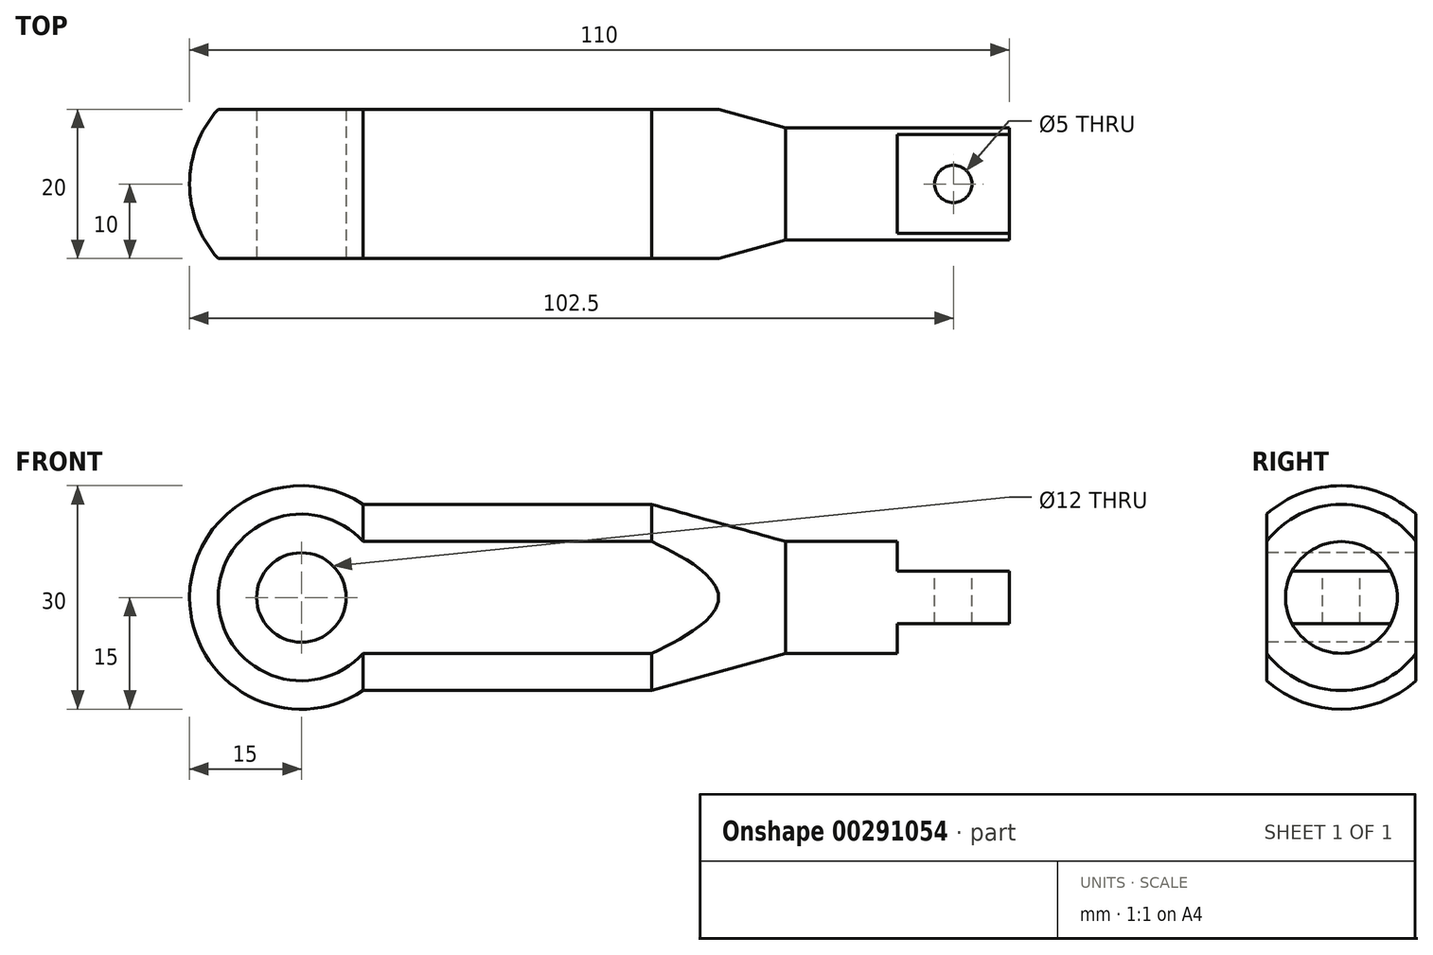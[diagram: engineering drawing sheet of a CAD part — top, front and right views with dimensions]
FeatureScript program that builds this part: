
annotation { "Feature Type Name" : "Feature", "Feature Type Description" : "" }
export const myFeature = defineFeature(function(context is Context, id is Id, definition is map)
    precondition{}
    {
        {
            var Q0;
            Q0=qCreatedBy(makeId("Front.planeOp"),FACE);
            var sketch = newSketch(context, id + "F0", { "sketchPlane" : qUnion([Q0])});
            skLineSegment(sketch, "E0", {"start": v(0, 0) * mm, "end": v(148.34, 0) * mm, "construction": true});
            skArc(sketch, "E1", {"start": v(-15, 0) * mm, "mid": v(-7.1, 13.22) * mm, "end": v(8.3, 12.5) * mm});
            skLineSegment(sketch, "E2", {"start": v(8.3, 12.5) * mm, "end": v(47, 12.5) * mm});
            skLineSegment(sketch, "E3", {"start": v(47, 12.5) * mm, "end": v(65, 7.5) * mm});
            skLineSegment(sketch, "E4", {"start": v(65, 7.5) * mm, "end": v(95, 7.5) * mm});
            skLineSegment(sketch, "E5", {"start": v(95, 7.5) * mm, "end": v(95, 0) * mm});
            skLineSegment(sketch, "E6", {"start": v(95, 0) * mm, "end": v(-15, 0) * mm});
            skSolve(sketch);
        }
        {
            var Q0;
            Q0 = qSketchRegion(id + "F0", true);
            var Q1;
            Q1=sQuery(id+"F0.wireOp",EDGE,"E0");
            revolve(context, id + "F1", {"entities" : qUnion([Q0]), "axis" : qUnion([Q1]), "revolveType" : RevolveType.FULL});
        }
        {
            var Q0;
            Q0=qCreatedBy(makeId("Front.planeOp"),FACE);
            var sketch = newSketch(context, id + "F2", { "sketchPlane" : qUnion([Q0])});
            skLineSegment(sketch, "E7", {"start": v(65, 7.5) * mm, "end": v(95, 7.5) * mm});
            skLineSegment(sketch, "E8.bottom", {"start": v(80, 7.5) * mm, "end": v(95, 7.5) * mm});
            skLineSegment(sketch, "E8.top", {"start": v(80, 3.5) * mm, "end": v(95, 3.5) * mm});
            skLineSegment(sketch, "E8.left", {"start": v(80, 7.5) * mm, "end": v(80, 3.5) * mm});
            skLineSegment(sketch, "E8.right", {"start": v(95, 7.5) * mm, "end": v(95, 3.5) * mm});
            skLineSegment(sketch, "E9", {"start": v(74.96, 0) * mm, "end": v(105.42, 0) * mm, "construction": true});
            skLineSegment(sketch, "E10.MirrorCS", {"start": v(95, -7.5) * mm, "end": v(95, -3.5) * mm});
            skLineSegment(sketch, "E11.MirrorCS", {"start": v(80, -7.5) * mm, "end": v(80, -3.5) * mm});
            skLineSegment(sketch, "E12.MirrorCS", {"start": v(80, -7.5) * mm, "end": v(95, -7.5) * mm});
            skLineSegment(sketch, "E13.MirrorCS", {"start": v(80, -3.5) * mm, "end": v(95, -3.5) * mm});
            skSolve(sketch);
        }
        {
            var Q0;
            Q0 = qSketchRegion(id + "F2", true);
            extrude(context, id + "F3", {"entities" : qUnion([Q0]), "operationType" : NewBodyOperationType.REMOVE, "endBound" : BoundingType.THROUGH_ALL, "oppositeDirection" : true, "depth" : 25 * mm, "hasSecondDirection" : true, "secondDirectionBound" : SecondDirectionBoundingType.THROUGH_ALL, "secondDirectionOppositeDirection" : false, "secondDirectionDepth" : 25 * mm});
        }
        {
            var Q0;
            Q0=makeQuery(id+"F1.opRevolve","SWEPT_FACE",FACE,{"disambiguationData":[OSD([sQuery(id+"F0.wireOp",EDGE,"E5")])]});
            var sketch = newSketch(context, id + "F4", { "sketchPlane" : qUnion([Q0])});
            skArc(sketch, "E14", {"start": v(-10, 11.18) * mm, "mid": v(-15, 0) * mm, "end": v(-10, -11.18) * mm});
            skLineSegment(sketch, "E15", {"start": v(-10, 11.18) * mm, "end": v(-10, -11.18) * mm});
            skLineSegment(sketch, "E16", {"start": v(10, 11.18) * mm, "end": v(10, -11.18) * mm});
            skLineSegment(sketch, "E17", {"start": v(0, 0) * mm, "end": v(0, 27.7) * mm, "construction": true});
            skArc(sketch, "E18.trimOffspring", {"start": v(10, -11.18) * mm, "mid": v(15, 0) * mm, "end": v(10, 11.18) * mm});
            skSolve(sketch);
        }
        {
            var Q0;
            Q0 = qSketchRegion(id + "F4", true);
            extrude(context, id + "F5", {"entities" : qUnion([Q0]), "operationType" : NewBodyOperationType.REMOVE, "endBound" : BoundingType.THROUGH_ALL, "oppositeDirection" : true, "depth" : 25 * mm});
        }
        {
            var Q0;
            Q0=makeQuery(id+"F5.boolean.opBoolean","COPY",FACE,{"derivedFrom":makeQuery(id+"F5.opExtrude","SWEPT_FACE",FACE,{"disambiguationData":[OSD([sQuery(id+"F4.wireOp",EDGE,"E15")])]})});
            var sketch = newSketch(context, id + "F6", { "sketchPlane" : qUnion([Q0])});
            skCircle(sketch, "E19", {"center": v(0, 0) * mm, "radius": 6 * mm});
            skSolve(sketch);
        }
        {
            var Q0;
            Q0 = qSketchRegion(id + "F6", true);
            extrude(context, id + "F7", {"entities" : qUnion([Q0]), "operationType" : NewBodyOperationType.REMOVE, "endBound" : BoundingType.THROUGH_ALL, "oppositeDirection" : true, "depth" : 25 * mm});
        }
        {
            var Q0;
            Q0=makeQuery(id+"F3.boolean.opBoolean","COPY",FACE,{"derivedFrom":makeQuery(id+"F3.opExtrude","SWEPT_FACE",FACE,{"disambiguationData":[OSD([sQuery(id+"F2.wireOp",EDGE,"E8.top")])]})});
            var sketch = newSketch(context, id + "F8", { "sketchPlane" : qUnion([Q0])});
            skCircle(sketch, "E20", {"center": v(87.5, 0) * mm, "radius": 2.5 * mm});
            skSolve(sketch);
        }
        {
            var Q0;
            Q0 = qSketchRegion(id + "F8", true);
            extrude(context, id + "F9", {"entities" : qUnion([Q0]), "operationType" : NewBodyOperationType.REMOVE, "endBound" : BoundingType.THROUGH_ALL, "oppositeDirection" : true, "depth" : 25 * mm});
        }
    });
